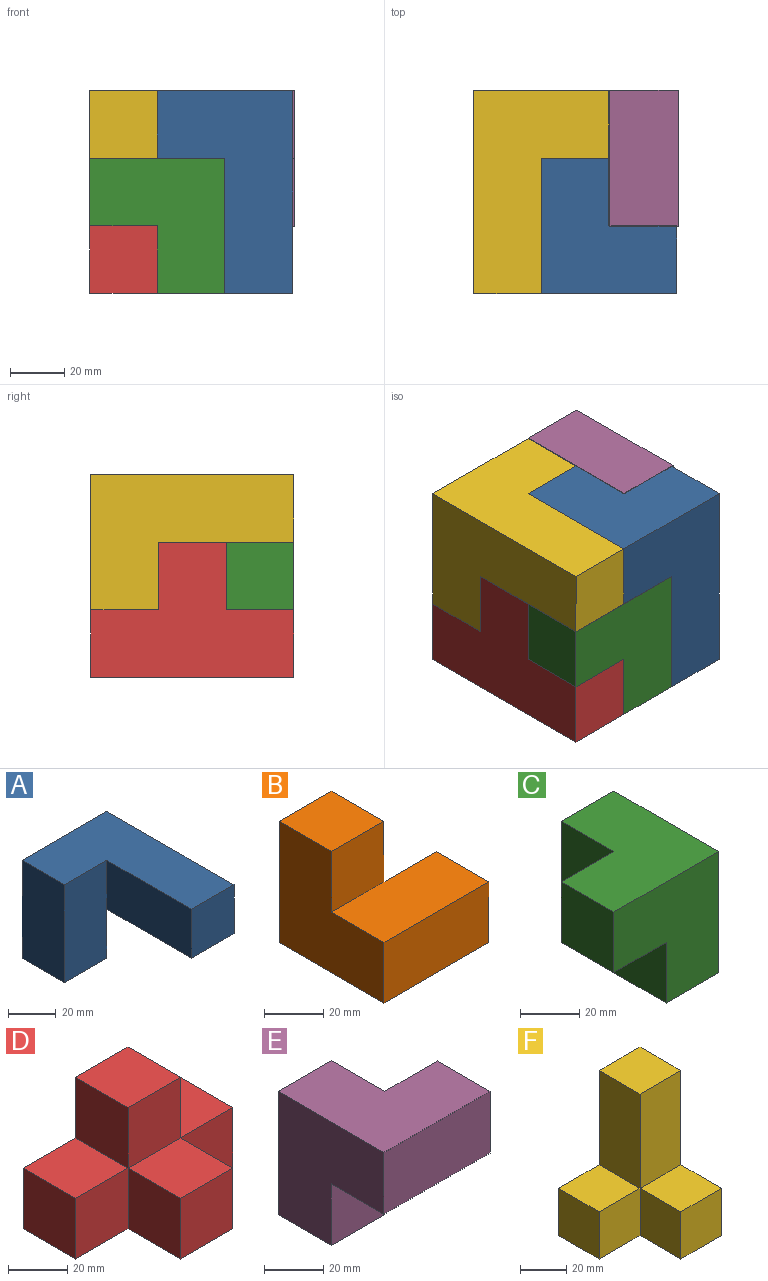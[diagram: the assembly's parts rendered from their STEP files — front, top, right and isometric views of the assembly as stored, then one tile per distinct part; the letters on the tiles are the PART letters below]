
ASSEMBLY  parts=6 mates=5
PART A: 10 faces, bbox 50x75x50 mm
  f0: plane 75x25mm, normal (0,0,-1), area 1875mm2, adj f3,f5,f6,f8,f9
  f1: plane 50x25mm, normal (-1,0,0), area 1250mm2, adj f2,f3,f4,f7
  f2: plane 50x25mm, normal (0,-1,0), area 1250mm2, adj f1,f4,f6,f7,f8
  f3: plane 50x50mm, normal (0,1,0), area 1875mm2, adj f0,f1,f4,f5,f6,f7
  f4: plane 75x50mm, normal (0,0,1), area 2500mm2, adj f1,f2,f3,f5,f8,f9
  f5: plane 75x25mm, normal (1,0,0), area 1875mm2, adj f0,f3,f4,f9
  f6: plane 25x25mm, normal (1,0,0), area 625mm2, adj f0,f2,f3,f7
  f7: plane 25x25mm, normal (0,0,-1), area 625mm2, adj f1,f2,f3,f6
  f8: plane 50x25mm, normal (-1,0,0), area 1250mm2, adj f0,f2,f4,f9
  f9: plane 25x25mm, normal (0,-1,0), area 625mm2, adj f0,f4,f5,f8
PART B: 10 faces, bbox 50x50x50 mm
  f0: plane 50x25mm, normal (0,0,1), area 1250mm2, adj f1,f2,f3,f5,f8
  f1: plane 25x25mm, normal (0,1,0), area 625mm2, adj f0,f3,f4,f6
  f2: plane 50x25mm, normal (0,-1,0), area 1250mm2, adj f0,f3,f4,f5
  f3: plane 25x25mm, normal (1,0,0), area 625mm2, adj f0,f1,f2,f4
  f4: plane 50x50mm, normal (0,0,-1), area 1875mm2, adj f1,f2,f3,f5,f6,f7
  f5: plane 50x50mm, normal (-1,0,0), area 1875mm2, adj f0,f2,f4,f7,f8,f9
  f6: plane 50x25mm, normal (1,0,0), area 1250mm2, adj f1,f4,f7,f8,f9
  f7: plane 50x25mm, normal (0,1,0), area 1250mm2, adj f4,f5,f6,f9
  f8: plane 25x25mm, normal (0,-1,0), area 625mm2, adj f0,f5,f6,f9
  f9: plane 25x25mm, normal (0,0,1), area 625mm2, adj f5,f6,f7,f8
PART C: 12 faces, bbox 50x50x50 mm
  f0: plane 25x25mm, normal (-1,0,0), area 625mm2, adj f3,f7,f8,f9
  f1: plane 25x25mm, normal (0,0,-1), area 625mm2, adj f2,f4,f6,f7
  f2: plane 25x25mm, normal (-1,0,0), area 625mm2, adj f1,f5,f6,f10
  f3: plane 50x50mm, normal (0,-1,0), area 1875mm2, adj f0,f4,f5,f8,f9,f11
  f4: plane 50x50mm, normal (1,0,0), area 1875mm2, adj f1,f3,f5,f6,f7,f8
  f5: plane 50x50mm, normal (0,0,1), area 1875mm2, adj f2,f3,f4,f6,f10,f11
  f6: plane 25x25mm, normal (0,1,0), area 625mm2, adj f1,f2,f4,f5
  f7: plane 25x25mm, normal (0,1,0), area 625mm2, adj f0,f1,f4,f8
  f8: plane 25x25mm, normal (0,0,-1), area 625mm2, adj f0,f3,f4,f7
  f9: plane 25x25mm, normal (0,0,-1), area 625mm2, adj f0,f3,f10,f11
  f10: plane 25x25mm, normal (0,1,0), area 625mm2, adj f2,f5,f9,f11
  f11: plane 25x25mm, normal (-1,0,0), area 625mm2, adj f3,f5,f9,f10
PART D: 16 faces, bbox 75x50x50 mm
  f0: plane 25x25mm, normal (1,0,0), area 625mm2, adj f4,f10,f12,f13
  f1: plane 25x25mm, normal (0,0,1), area 625mm2, adj f2,f3,f7,f10
  f2: plane 25x25mm, normal (-1,0,0), area 625mm2, adj f1,f6,f7,f8
  f3: plane 25x25mm, normal (1,0,0), area 625mm2, adj f1,f6,f7,f14
  f4: plane 75x50mm, normal (0,1,0), area 2500mm2, adj f0,f5,f6,f9,f11,f12,f13,f15
  f5: plane 25x25mm, normal (0,0,1), area 625mm2, adj f4,f8,f9,f11
  f6: plane 75x50mm, normal (0,0,-1), area 2500mm2, adj f2,f3,f4,f7,f8,f9,f14,f15
  f7: plane 25x25mm, normal (0,-1,0), area 625mm2, adj f1,f2,f3,f6
  f8: plane 25x25mm, normal (0,-1,0), area 625mm2, adj f2,f5,f6,f9
  f9: plane 25x25mm, normal (-1,0,0), area 625mm2, adj f4,f5,f6,f8
  f10: plane 25x25mm, normal (0,-1,0), area 625mm2, adj f0,f1,f11,f12
  f11: plane 25x25mm, normal (-1,0,0), area 625mm2, adj f4,f5,f10,f12
  f12: plane 25x25mm, normal (0,0,1), area 625mm2, adj f0,f4,f10,f11
  f13: plane 25x25mm, normal (0,0,1), area 625mm2, adj f0,f4,f14,f15
  f14: plane 25x25mm, normal (0,-1,0), area 625mm2, adj f3,f6,f13,f15
  f15: plane 25x25mm, normal (1,0,0), area 625mm2, adj f4,f6,f13,f14
PART E: 10 faces, bbox 50.4x50.4x50.8 mm
  f0: plane 50.4x25mm, normal (0,0,-1), area 1260mm2, adj f1,f2,f3,f5,f8
  f1: plane 50.4x25.4mm, normal (0,-1,0), area 1280.2mm2, adj f0,f2,f4,f5
  f2: plane 25.4x25mm, normal (1,0,0), area 635mm2, adj f0,f1,f3,f4
  f3: plane 25.4x25mm, normal (0,1,0), area 635mm2, adj f0,f2,f4,f6
  f4: plane 50.4x50.4mm, normal (0,0,1), area 1905.2mm2, adj f1,f2,f3,f5,f6,f7
  f5: plane 50.8x50.4mm, normal (-1,0,0), area 1925.3mm2, adj f0,f1,f4,f7,f8,f9
  f6: plane 50.8x25.4mm, normal (1,0,0), area 1290.3mm2, adj f3,f4,f7,f8,f9
  f7: plane 50.8x25.4mm, normal (0,1,0), area 1290.3mm2, adj f4,f5,f6,f9
  f8: plane 25.4x25.4mm, normal (0,-1,0), area 645.2mm2, adj f0,f5,f6,f9
  f9: plane 25.4x25.4mm, normal (0,0,-1), area 645.2mm2, adj f5,f6,f7,f8
PART F: 12 faces, bbox 50x50x75 mm
  f0: plane 25x25mm, normal (0,-1,0), area 625mm2, adj f5,f6,f7,f10
  f1: plane 50x25mm, normal (-1,0,0), area 1250mm2, adj f2,f3,f6,f8
  f2: plane 75x50mm, normal (0,1,0), area 2500mm2, adj f1,f4,f5,f6,f7,f8
  f3: plane 50x25mm, normal (0,-1,0), area 1250mm2, adj f1,f4,f8,f9
  f4: plane 75x50mm, normal (1,0,0), area 2500mm2, adj f2,f3,f5,f8,f9,f11
  f5: plane 50x50mm, normal (0,0,-1), area 1875mm2, adj f0,f2,f4,f7,f10,f11
  f6: plane 25x25mm, normal (0,0,1), area 625mm2, adj f0,f1,f2,f7
  f7: plane 25x25mm, normal (-1,0,0), area 625mm2, adj f0,f2,f5,f6
  f8: plane 25x25mm, normal (0,0,1), area 625mm2, adj f1,f2,f3,f4
  f9: plane 25x25mm, normal (0,0,1), area 625mm2, adj f3,f4,f10,f11
  f10: plane 25x25mm, normal (-1,0,0), area 625mm2, adj f0,f5,f9,f11
  f11: plane 25x25mm, normal (0,-1,0), area 625mm2, adj f4,f5,f9,f10
PLACE A rot(axis=(1,0,0),90deg) t=(-10.92,-70.25,37.83)mm
PLACE B rot(axis=(0,0,-1),180deg) t=(14.08,-20.25,-12.17)mm
PLACE C t=(-10.92,-70.25,12.83)mm
PLACE D rot(axis=(0,0,1),90deg) t=(-10.92,-45.25,-12.17)mm
PLACE E rot(axis=(-0.58,0.58,-0.58),120deg) t=(39.68,-20.45,62.83)mm
PLACE F rot(axis=(0.58,-0.58,0.58),120deg) t=(-35.92,-20.25,37.83)mm
MATE fastened E.f8 <-> F.f10  axis (0,0,1) through (1.58,-7.75,37.83)mm
MATE fastened D.f13 <-> F.f7  axis (0,0,1) through (-23.42,-7.75,12.83)mm
MATE fastened F.f9 <-> A.f7  axis (0,-1,0) through (1.58,-20.25,50.33)mm
MATE fastened D.f14 <-> B.f3  axis (1,0,0) through (-10.92,-7.75,0.33)mm
MATE fastened D.f5 <-> C.f9  axis (0,0,1) through (-23.42,-57.75,12.83)mm
